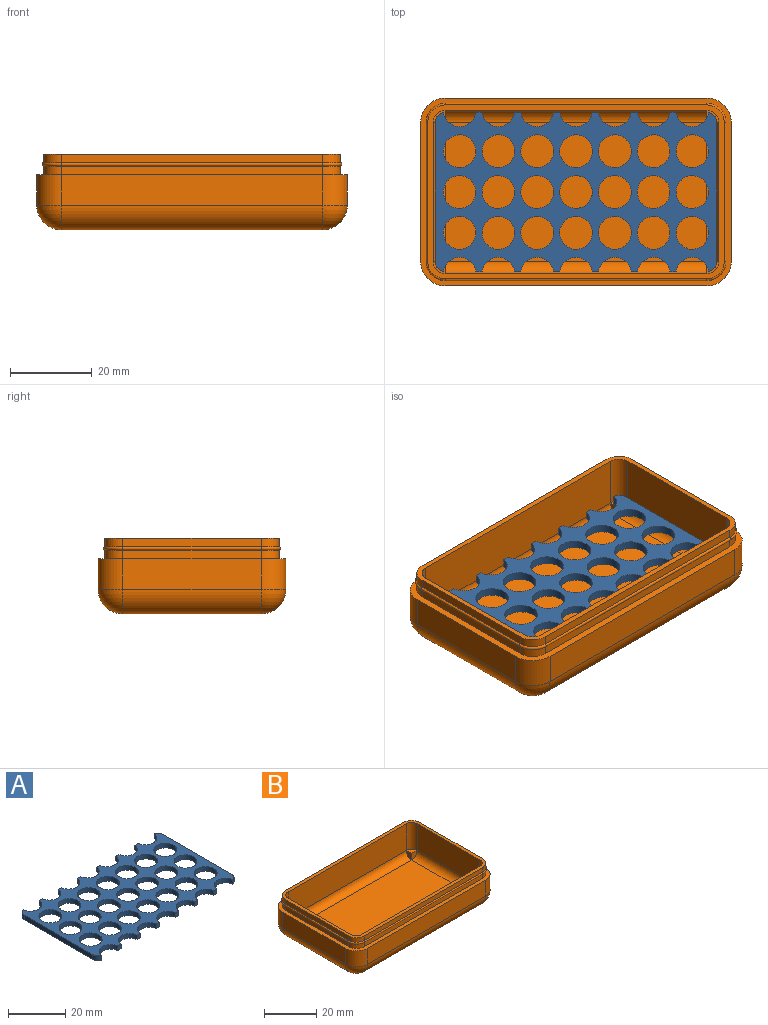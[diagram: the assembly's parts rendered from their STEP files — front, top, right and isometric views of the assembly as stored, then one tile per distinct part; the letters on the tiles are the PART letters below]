
ASSEMBLY  parts=2 mates=1
PART A: 55 faces, bbox 69x39x2 mm
  f0: plane 2x1.56mm, normal (0,1,0), area 3.1mm2, adj f11,f12,f52,f53
  f1: plane 2x1.56mm, normal (0,1,0), area 3.1mm2, adj f12,f13,f52,f53
  f2: plane 2x1.56mm, normal (0,1,0), area 3.1mm2, adj f13,f14,f52,f53
  f3: plane 2x1.56mm, normal (0,1,0), area 3.1mm2, adj f14,f15,f52,f53
  f4: plane 2x1.56mm, normal (0,1,0), area 3.1mm2, adj f15,f16,f52,f53
  f5: plane 2x1.56mm, normal (0,-1,0), area 3.1mm2, adj f38,f39,f52,f53
  f6: plane 2x1.56mm, normal (0,-1,0), area 3.1mm2, adj f39,f40,f52,f53
  f7: plane 2x1.56mm, normal (0,-1,0), area 3.1mm2, adj f40,f41,f52,f53
  f8: plane 2x1.56mm, normal (0,-1,0), area 3.1mm2, adj f41,f42,f52,f53
  f9: plane 2x1.56mm, normal (0,-1,0), area 3.1mm2, adj f42,f43,f52,f53
  f10: cylinder r=4mm len=7.93mm, axis (0,0,-1), area 23mm2, adj f47,f48,f52,f53
  f11: cylinder r=4mm len=7.94mm, axis (0,0,-1), area 23.1mm2, adj f0,f48,f52,f53
  f12: cylinder r=4mm len=7.94mm, axis (0,0,-1), area 23.1mm2, adj f0,f1,f52,f53
  f13: cylinder r=4mm len=7.94mm, axis (0,0,-1), area 23.1mm2, adj f1,f2,f52,f53
  f14: cylinder r=4mm len=7.94mm, axis (0,0,-1), area 23.1mm2, adj f2,f3,f52,f53
  f15: cylinder r=4mm len=7.94mm, axis (0,0,-1), area 23.1mm2, adj f3,f4,f52,f53
  f16: cylinder r=4mm len=7.93mm, axis (0,0,-1), area 23mm2, adj f4,f49,f52,f53
  f17: cylinder r=4mm len=8mm, axis (0,0,-1), area 50.3mm2, adj f52,f53
  f18: cylinder r=4mm len=8mm, axis (0,0,-1), area 50.3mm2, adj f52,f53
  f19: cylinder r=4mm len=8mm, axis (0,0,-1), area 50.3mm2, adj f52,f53
  f20: cylinder r=4mm len=8mm, axis (0,0,-1), area 50.3mm2, adj f52,f53
  f21: cylinder r=4mm len=8mm, axis (0,0,-1), area 50.3mm2, adj f52,f53
  f22: cylinder r=4mm len=8mm, axis (0,0,-1), area 50.3mm2, adj f52,f53
  f23: cylinder r=4mm len=8mm, axis (0,0,-1), area 50.3mm2, adj f52,f53
  f24: cylinder r=4mm len=8mm, axis (0,0,-1), area 50.3mm2, adj f52,f53
  f25: cylinder r=4mm len=8mm, axis (0,0,-1), area 50.3mm2, adj f52,f53
  f26: cylinder r=4mm len=8mm, axis (0,0,-1), area 50.3mm2, adj f52,f53
  f27: cylinder r=4mm len=8mm, axis (0,0,-1), area 50.3mm2, adj f52,f53
  f28: cylinder r=4mm len=8mm, axis (0,0,-1), area 50.3mm2, adj f52,f53
  f29: cylinder r=4mm len=8mm, axis (0,0,-1), area 50.3mm2, adj f52,f53
  f30: cylinder r=4mm len=8mm, axis (0,0,-1), area 50.3mm2, adj f52,f53
  f31: cylinder r=4mm len=8mm, axis (0,0,-1), area 50.3mm2, adj f52,f53
  f32: cylinder r=4mm len=8mm, axis (0,0,-1), area 50.3mm2, adj f52,f53
  f33: cylinder r=4mm len=8mm, axis (0,0,-1), area 50.3mm2, adj f52,f53
  f34: cylinder r=4mm len=8mm, axis (0,0,-1), area 50.3mm2, adj f52,f53
  f35: cylinder r=4mm len=8mm, axis (0,0,-1), area 50.3mm2, adj f52,f53
  f36: cylinder r=4mm len=8mm, axis (0,0,-1), area 50.3mm2, adj f52,f53
  f37: cylinder r=4mm len=7.93mm, axis (0,0,-1), area 23mm2, adj f44,f45,f52,f53
  f38: cylinder r=4mm len=7.94mm, axis (0,0,-1), area 23.1mm2, adj f5,f44,f52,f53
  f39: cylinder r=4mm len=7.94mm, axis (0,0,-1), area 23.1mm2, adj f5,f6,f52,f53
  f40: cylinder r=4mm len=7.94mm, axis (0,0,-1), area 23.1mm2, adj f6,f7,f52,f53
  f41: cylinder r=4mm len=7.94mm, axis (0,0,-1), area 23.1mm2, adj f7,f8,f52,f53
  f42: cylinder r=4mm len=7.94mm, axis (0,0,-1), area 23.1mm2, adj f8,f9,f52,f53
  f43: cylinder r=4mm len=7.93mm, axis (0,0,-1), area 23mm2, adj f9,f51,f52,f53
  f44: plane 2x1.56mm, normal (0,-1,0), area 3.1mm2, adj f37,f38,f52,f53
  f45: cylinder r=2.5mm len=2.46mm, axis (0,0,1), area 6.9mm2, adj f37,f46,f52,f53
  f46: plane 34x2mm, normal (1,0,0), area 68mm2, adj f45,f47,f52,f53
  f47: cylinder r=2.5mm len=2.46mm, axis (0,0,1), area 6.9mm2, adj f10,f46,f52,f53
  f48: plane 2x1.56mm, normal (0,1,0), area 3.1mm2, adj f10,f11,f52,f53
  f49: cylinder r=2.5mm len=2.46mm, axis (0,0,1), area 6.9mm2, adj f16,f50,f52,f53
  f50: plane 34x2mm, normal (-1,0,0), area 68mm2, adj f49,f51,f52,f53
  f51: cylinder r=2.5mm len=2.46mm, axis (0,0,1), area 6.9mm2, adj f43,f50,f52,f53
  f52: plane 69x39mm, normal (0,0,-1), area 1334.1mm2, adj f0,f1,f2,f3,f4,f5,f6,f7
  f53: plane 69x39mm, normal (0,0,1), area 1334.1mm2, adj f0,f1,f2,f3,f4,f5,f6,f7
  f54: cylinder r=4mm len=8mm, axis (0,0,-1), area 50.3mm2, adj f52,f53
PART B: 68 faces, bbox 76x46x18.5 mm
  f0: cylinder r=4.3mm len=4.3mm, axis (0,0,1), area 14.2mm2, adj f1,f7,f8,f28
  f1: plane 64x2.1mm, normal (0,1,0), area 134.4mm2, adj f0,f2,f8,f29
  f2: cylinder r=4.3mm len=4.3mm, axis (0,0,1), area 14.2mm2, adj f1,f3,f8,f30
  f3: plane 34x2.1mm, normal (1,0,0), area 71.4mm2, adj f2,f4,f8,f31
  f4: cylinder r=4.3mm len=4.3mm, axis (0,0,1), area 14.2mm2, adj f3,f5,f8,f32
  f5: plane 64x2.1mm, normal (0,-1,0), area 134.4mm2, adj f4,f6,f8,f33
  f6: cylinder r=4.3mm len=4.3mm, axis (0,0,1), area 14.2mm2, adj f5,f7,f8,f26
  f7: plane 34x2.1mm, normal (-1,0,0), area 71.4mm2, adj f0,f6,f8,f27
  f8: plane 76x46mm, normal (0,0,1), area 388.2mm2, adj f0,f1,f2,f3,f4,f5,f6,f7
  f9: plane 64x34mm, normal (0,0,-1), area 2176mm2, adj f10,f11,f12,f13
  f10: cylinder r=6mm len=64mm, axis (-1,0,0), area 603.2mm2, adj f9,f16,f17,f25
  f11: cylinder r=6mm len=34mm, axis (0,-1,0), area 320.4mm2, adj f9,f15,f17,f24
  f12: cylinder r=6mm len=64mm, axis (1,0,0), area 603.2mm2, adj f9,f14,f15,f22
  f13: cylinder r=6mm len=34mm, axis (0,1,0), area 320.4mm2, adj f9,f14,f16,f20
  f14: sphere r=6mm, area 56.5mm2, adj f12,f13,f18
  f15: sphere r=6mm, area 56.5mm2, adj f11,f12,f21
  f16: sphere r=6mm, area 56.5mm2, adj f10,f13,f19
  f17: sphere r=6mm, area 56.5mm2, adj f10,f11,f23
  f18: cylinder r=6mm len=7.5mm, axis (0,0,1), area 70.7mm2, adj f8,f14,f20,f22
  f19: cylinder r=6mm len=7.5mm, axis (0,0,-1), area 70.7mm2, adj f8,f16,f20,f25
  f20: plane 34x7.5mm, normal (1,0,0), area 255mm2, adj f8,f13,f18,f19
  f21: cylinder r=6mm len=7.5mm, axis (0,0,-1), area 70.7mm2, adj f8,f15,f22,f24
  f22: plane 64x7.5mm, normal (0,-1,0), area 480mm2, adj f8,f12,f18,f21
  f23: cylinder r=6mm len=7.5mm, axis (0,0,1), area 70.7mm2, adj f8,f17,f24,f25
  f24: plane 34x7.5mm, normal (-1,0,0), area 255mm2, adj f8,f11,f21,f23
  f25: plane 64x7.5mm, normal (0,1,0), area 480mm2, adj f8,f10,f19,f23
  f26: torus R=4.3mm, axis (0,0,1), area 9mm2, adj f6,f27,f33,f61
  f27: cylinder r=0.4mm len=34mm, axis (0,-1,0), area 42.7mm2, adj f7,f26,f28,f60
  f28: torus R=4.3mm, axis (0,0,1), area 9mm2, adj f0,f27,f29,f67
  f29: cylinder r=0.4mm len=64mm, axis (-1,0,0), area 80.4mm2, adj f1,f28,f30,f66
  f30: torus R=4.3mm, axis (0,0,1), area 9mm2, adj f2,f29,f31,f65
  f31: cylinder r=0.4mm len=34mm, axis (0,1,0), area 42.7mm2, adj f3,f30,f32,f64
  f32: torus R=4.3mm, axis (0,0,1), area 9mm2, adj f4,f31,f33,f63
  f33: cylinder r=0.4mm len=64mm, axis (1,0,0), area 80.4mm2, adj f5,f26,f32,f62
  f34: plane 3x3mm, normal (0,1,0), area 7.1mm2, adj f35,f43,f44
  f35: plane 3x3mm, normal (1,0,0), area 7.1mm2, adj f34,f44,f45
  f36: plane 3x3mm, normal (-1,0,0), area 7.1mm2, adj f37,f45,f46
  f37: plane 3x3mm, normal (0,1,0), area 7.1mm2, adj f36,f46,f47
  f38: plane 3x3mm, normal (0,-1,0), area 7.1mm2, adj f40,f47,f48
  f39: plane 64x34mm, normal (0,0,1), area 2176mm2, adj f43,f45,f47,f49
  f40: plane 3x3mm, normal (-1,0,0), area 7.1mm2, adj f38,f48,f49
  f41: plane 3x3mm, normal (0,-1,0), area 7.1mm2, adj f42,f43,f50
  f42: plane 3x3mm, normal (1,0,0), area 7.1mm2, adj f41,f49,f50
  f43: cylinder r=3mm len=34mm, axis (0,-1,0), area 160.2mm2, adj f34,f39,f41,f51
  f44: plane 3x3mm, normal (0,0,1), area 7.1mm2, adj f34,f35,f52
  f45: cylinder r=3mm len=64mm, axis (1,0,0), area 301.6mm2, adj f35,f36,f39,f53
  f46: plane 3x3mm, normal (0,0,1), area 7.1mm2, adj f36,f37,f54
  f47: cylinder r=3mm len=34mm, axis (0,1,0), area 160.2mm2, adj f37,f38,f39,f55
  f48: plane 3x3mm, normal (0,0,1), area 7.1mm2, adj f38,f40,f56
  f49: cylinder r=3mm len=64mm, axis (-1,0,0), area 301.6mm2, adj f39,f40,f42,f57
  f50: plane 3x3mm, normal (0,0,1), area 7.1mm2, adj f41,f42,f58
  f51: plane 34x12.5mm, normal (1,0,0), area 425mm2, adj f43,f52,f58,f59
  f52: cylinder r=3mm len=12.5mm, axis (0,0,-1), area 58.9mm2, adj f44,f51,f53,f59
  f53: plane 64x12.5mm, normal (0,1,0), area 800mm2, adj f45,f52,f54,f59
  f54: cylinder r=3mm len=12.5mm, axis (0,0,1), area 58.9mm2, adj f46,f53,f55,f59
  f55: plane 34x12.5mm, normal (-1,0,0), area 425mm2, adj f47,f54,f56,f59
  f56: cylinder r=3mm len=12.5mm, axis (0,0,-1), area 58.9mm2, adj f48,f55,f57,f59
  f57: plane 64x12.5mm, normal (0,-1,0), area 800mm2, adj f49,f56,f58,f59
  f58: cylinder r=3mm len=12.5mm, axis (0,0,1), area 58.9mm2, adj f50,f51,f57,f59
  f59: plane 72.6x42.6mm, normal (0,0,1), area 284.6mm2, adj f51,f52,f53,f54,f55,f56,f57,f58
  f60: plane 34x2.1mm, normal (-1,0,0), area 71.4mm2, adj f27,f59,f61,f67
  f61: cylinder r=4.3mm len=4.3mm, axis (0,0,1), area 14.2mm2, adj f26,f59,f60,f62
  f62: plane 64x2.1mm, normal (0,-1,0), area 134.4mm2, adj f33,f59,f61,f63
  f63: cylinder r=4.3mm len=4.3mm, axis (0,0,1), area 14.2mm2, adj f32,f59,f62,f64
  f64: plane 34x2.1mm, normal (1,0,0), area 71.4mm2, adj f31,f59,f63,f65
  f65: cylinder r=4.3mm len=4.3mm, axis (0,0,1), area 14.2mm2, adj f30,f59,f64,f66
  f66: plane 64x2.1mm, normal (0,1,0), area 134.4mm2, adj f29,f59,f65,f67
  f67: cylinder r=4.3mm len=4.3mm, axis (0,0,1), area 14.2mm2, adj f28,f59,f60,f66
PLACE A rot(axis=(1,0,0),180deg) t=(0,0,0)mm
PLACE B at identity
MATE fastened B.f9 <-> A.f54  axis (0,0,-1) through (0,0,0)mm
